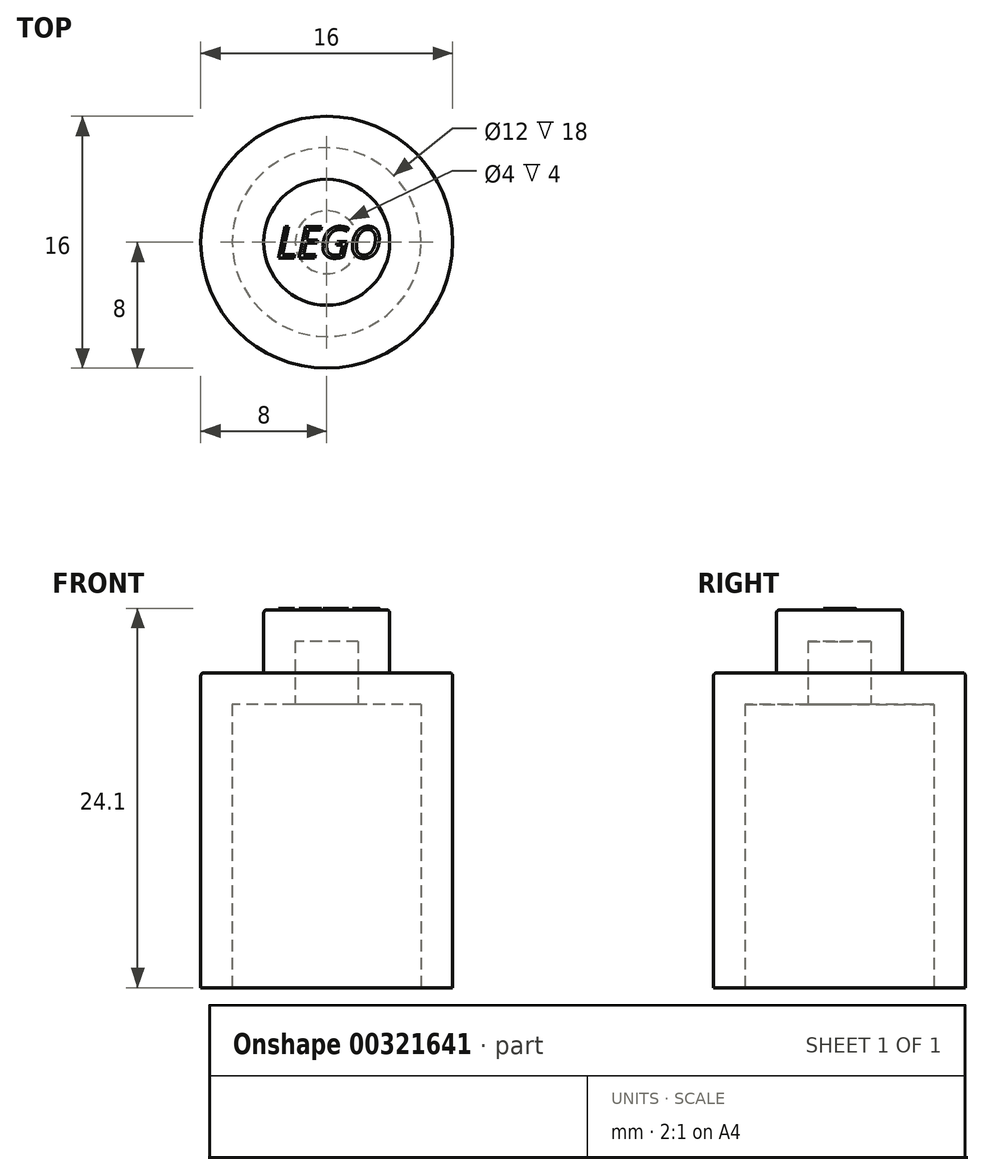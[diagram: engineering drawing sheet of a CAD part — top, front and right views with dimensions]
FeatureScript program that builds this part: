
annotation { "Feature Type Name" : "Feature", "Feature Type Description" : "" }
export const myFeature = defineFeature(function(context is Context, id is Id, definition is map)
    precondition{}
    {
        {
            var Q0;
            Q0=qCreatedBy(makeId("Top.planeOp"),FACE);
            var sketch = newSketch(context, id + "F0", { "sketchPlane" : qUnion([Q0])});
            skPoint(sketch, "E0.middle", {"position": v(0, 0) * mm});
            skCircle(sketch, "E1", {"center": v(-8, 0) * mm, "radius": 8 * mm});
            skPoint(sketch, "E1.centerSnap0", {"position": v(-16, 0) * mm});
            skSolve(sketch);
        }
        {
            var Q0;
            Q0=makeQuery(id+"F0.imprint","IMPRINT",FACE,{"disambiguationData":[TD([[makeQuery(id+"F0.imprint","IMPRINT",EDGE,{"derivedFrom":sQuery(id+"F0.wireOp",EDGE,"E1")}),1.0]])]});
            extrude(context, id + "F1", {"entities" : qUnion([Q0]), "offsetDistance" : 25 * mm, "depth" : 20 * mm});
        }
        {
            var Q0;
            Q0=makeQuery(id+"F1.opExtrude","CAP_FACE",FACE,{"disambiguationData":[OSD([sQuery(id+"F0.wireOp",EDGE,"E1")])],"isStart":false});
            var sketch = newSketch(context, id + "F2", { "sketchPlane" : qUnion([Q0])});
            skCircle(sketch, "E2", {"center": v(-8, 0) * mm, "radius": 4 * mm});
            skSolve(sketch);
        }
        {
            var Q0;
            Q0=makeQuery(id+"F2.imprint","IMPRINT",FACE,{"disambiguationData":[TD([[makeQuery(id+"F2.imprint","IMPRINT",EDGE,{"derivedFrom":sQuery(id+"F2.wireOp",EDGE,"E2")}),1.0]])]});
            extrude(context, id + "F3", {"entities" : qUnion([Q0]), "operationType" : NewBodyOperationType.ADD, "depth" : 4 * mm, "offsetDistance" : 25 * mm});
        }
        {
            var Q0;
            Q0=makeQuery(id+"F1.opExtrude","CAP_FACE",FACE,{"disambiguationData":[OSD([sQuery(id+"F0.wireOp",EDGE,"E1")])],"isStart":true});
            shell(context, id + "F4", {"entities" : qUnion([Q0]), "thickness" : 2 * mm});
        }
        {
            var Q0;
            Q0=makeQuery(id+"F1.opExtrude","CAP_EDGE",EDGE,{"disambiguationData":[OSD([sQuery(id+"F0.wireOp",EDGE,"E1")])],"isStart":false});
            var Q1;
            Q1=makeQuery(id+"F3.opExtrude","CAP_EDGE",EDGE,{"disambiguationData":[OSD([sQuery(id+"F2.wireOp",EDGE,"E2")])],"isStart":false});
            fillet(context, id + "F5", {"entities" : qUnion([Q0, Q1]), "radius" : 0.2 * mm, "tangentPropagation" : true, "defaultsChanged" : false, "vertexSettings" : [], "allowEdgeOverflow" : false});
        }
        {
            var Q0;
            Q0=makeQuery(id+"F3.opExtrude","CAP_FACE",FACE,{"disambiguationData":[OSD([sQuery(id+"F2.wireOp",EDGE,"E2")])],"isStart":false});
            var sketch = newSketch(context, id + "F6", { "sketchPlane" : qUnion([Q0])});
            skText(sketch, "E3", { "text": "LEGO", "fontName": "OpenSans-Italic.ttf"});
            const initialGuessF6  = {"E3": [-0.01119, -0.001, 1, 0, 0.002]};
            skSetInitialGuess(sketch, initialGuessF6);
            skSolve(sketch);
        }
        {
            var Q0;
            Q0 = qSketchRegion(id + "F6", true);
            extrude(context, id + "F7", {"entities" : qUnion([Q0]), "operationType" : NewBodyOperationType.ADD, "depth" : 0.1 * mm, "offsetDistance" : 25 * mm});
        }
    });
